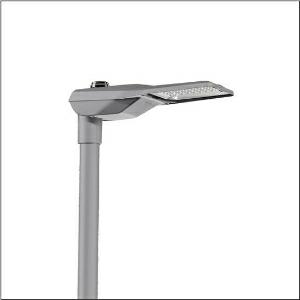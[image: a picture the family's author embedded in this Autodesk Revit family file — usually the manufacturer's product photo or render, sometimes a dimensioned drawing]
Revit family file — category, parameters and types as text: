
# Revit family: streetlight_sl_21_mini___st1_0a_5xe6d47n08jb_8270
name_source: partatom
category: Lighting Fixtures
units: mm (PartAtom-declared; Revit-internal decimal feet)

## family parameters
Cut with Voids When Loaded = No
Host = Face
Light Source = No
Part Type = Normal
Room Calculation Point = No
Round Connector Dimension = Use Diameter
Shared = No

## types (1)
- --- (1 x LED, 13390 lm, 87.3 W, 4000K)
    Apparent Load = 87 VA
    CIE Flux Codes = 40 73 97 100 100
    Color Rendering = 70
    Color Temperature = 4000K
    Default Elevation = 1800 mm
    Description = Streetlight SL 21 mini, mast luminaire, primary light control with lens, of PMMA, primary optical cover: cover, of toughened safety glass, transparent, light distribution: ST1.0a, light emission: direct distribution, primary light characteristic: asymmetric, installation type: side-entry, LED, 3G 2.5mm², High Power LED, rated luminous flux: 13.390lm, luminous efficacy: 153lm/W, light colour: 740, colour temperature: 4000K, control gear: NEMA (7pin), control: overheat protection, pre-setting: linear dimming characteristic, constant luminous flux control, time-dependent luminous flux control, flexible luminous flux parameterisation, mains connection: 230..240V, AC, 50/60Hz, connection cable pre-assembled, cable length: 10,5m, wiring characteristics: H05VV-F, start of lifetime: 87W, end of service life: 90W, reduction: 40W, luminaire housing, of diecast aluminium (EN AC-44300), powder-coated, Siteco® metallic grey (DB 702S), corrosivity category C5 mid according to DIN EN ISO 12944, multi-level sealing system, sealing non-destructively replaceable, inclination adjustable: 0°, 5°, 10°, 15°, length: 628mm, width: 235mm, height: 110mm, spigot size: 42mm (side-entry), mounting height: 4..8m, protection rating (complete): IP66, insulation class (complete): insulation class I (protective earthing), certification: CE, ENEC, ENEC+, VDE, impact resistance: IK10, permissible operating ambient temperature for outdoor applications: -40..+50°C, standard-compliant lighting for roads and squares, packaging unit: 1 piece

Light Distribution: ST1.0a
    Height = 110 mm
    Lamp = 1 x LED
    Lamp Light Flux = 13390 lm
    Lamp Power = 87.3 W
    Lamp count = 1
    Length = 625 mm
    Luminous efficacy = 153 lm/W
    Manufacturer = Siteco
    ModVariant = No
    Model = 5XE6D47N08JB
    Number of Poles = 1
    OnlyDefault = Yes
    Power Factor = 1
    Product Name = Streetlight SL 21 mini | ST1.0a
    Product group = mast luminaire | pylon top
    ProductGroupID = 6100
    Protection Class = Protection class I
    Protection Degree = IP 66
    RLX_Detail_Level = 1
    RLX_Emergency_Light_Flux = 0 lm
    RLX_Emergency_Type = 0
    RLX_Emergency_Type_DB = No
    RlxData = <blob elided: 26069 chars, md5=88ae03bc>
    Socket = socket
    Standby Power = 0 W
    System Light Flux = 13390 lm
    System Power = 87 W
    Type Comments = factory setting: luminous flux: 100 % | dim-lin: 254 | 915 mA
    Type Image = l_1294379.jpg
    URL = http://relux.com
    VarID = @adj_156801
    Voltage = 0 V
    Weight = 0.00 kg
    Width = 234 mm

## geometry (parser evidence)
native form markers: Blend x4, Sweep x14
no freeform markers — native parametric forms only
